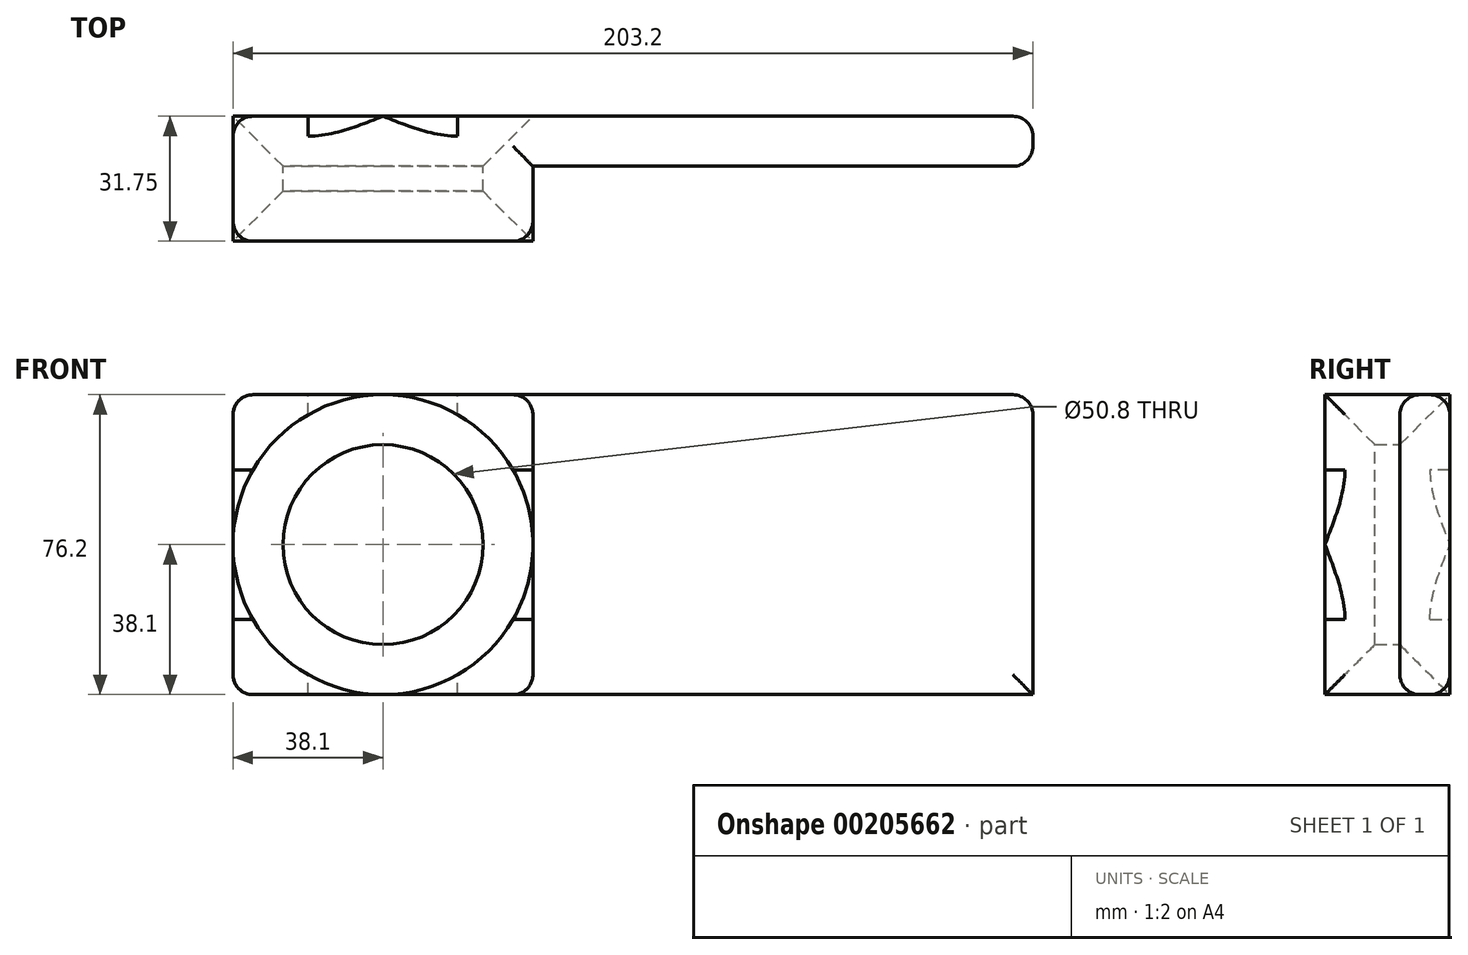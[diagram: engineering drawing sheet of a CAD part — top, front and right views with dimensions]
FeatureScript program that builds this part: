
annotation { "Feature Type Name" : "Feature", "Feature Type Description" : "" }
export const myFeature = defineFeature(function(context is Context, id is Id, definition is map)
    precondition{}
    {
        {
            var Q0;
            Q0=qCreatedBy(makeId("Front.planeOp"),FACE);
            var sketch = newSketch(context, id + "F0", { "sketchPlane" : qUnion([Q0])});
            skLineSegment(sketch, "E0.bottom", {"start": v(101.6, 38.1) * mm, "end": v(-101.6, 38.1) * mm});
            skLineSegment(sketch, "E0.top", {"start": v(101.6, -38.1) * mm, "end": v(-101.6, -38.1) * mm});
            skLineSegment(sketch, "E0.left", {"start": v(101.6, 38.1) * mm, "end": v(101.6, -38.1) * mm});
            skLineSegment(sketch, "E0.right", {"start": v(-101.6, 38.1) * mm, "end": v(-101.6, -38.1) * mm});
            skPoint(sketch, "E0.middle", {"position": v(0, 0) * mm});
            skLineSegment(sketch, "E1", {"start": v(-101.6, 0) * mm, "end": v(101.6, 0) * mm, "construction": true});
            skLineSegment(sketch, "E2", {"start": v(-63.5, 38.1) * mm, "end": v(-63.5, -38.1) * mm, "construction": true});
            skLineSegment(sketch, "E3.bottom", {"start": v(-25.4, 38.1) * mm, "end": v(-101.6, 38.1) * mm});
            skLineSegment(sketch, "E3.top", {"start": v(-25.4, -38.1) * mm, "end": v(-101.6, -38.1) * mm});
            skPoint(sketch, "E3.middle", {"position": v(-63.5, 0) * mm});
            skCircle(sketch, "E4", {"center": v(-63.5, 0) * mm, "radius": 25.4 * mm});
            skLineSegment(sketch, "E5.left", {"start": v(-25.4, 38.1) * mm, "end": v(-25.4, -38.1) * mm});
            skSolve(sketch);
        }
        {
            var Q0;
            Q0 = qSketchRegion(id + "F0", true);
            extrude(context, id + "F1", {"entities" : qUnion([Q0]), "endBound" : BoundingType.SYMMETRIC, "depth" : 12.7 * mm});
        }
        {
            var Q0;
            Q0=makeQuery(id+"F0.imprint","IMPRINT",FACE,{"disambiguationData":[TD([[makeQuery(id+"F0.imprint","IMPRINT",EDGE,{"derivedFrom":sQuery(id+"F0.wireOp",EDGE,"E4")}),-1.0]])]});
            extrude(context, id + "F2", {"entities" : qUnion([Q0]), "operationType" : NewBodyOperationType.ADD, "depth" : 25.4 * mm});
        }
        {
            var Q0;
            Q0=makeQuery(id+"F2.opExtrude","CAP_EDGE",EDGE,{"disambiguationData":[OSD([sQuery(id+"F0.wireOp",EDGE,"E4")])],"isStart":false});
            var Q1;
            Q1=makeQuery(id+"F1.opExtrude","CAP_EDGE",EDGE,{"disambiguationData":[OSD([sQuery(id+"F0.wireOp",EDGE,"E4")])],"isStart":true});
            chamfer(context, id + "F3", {"entities" : qUnion([Q0, Q1]), "width" : 12.7 * mm, "tangentPropagation" : true});
        }
        {
            var Q0;
            Q0=makeQuery(id+"F2.opExtrude","CAP_EDGE",EDGE,{"disambiguationData":[OSD([sQuery(id+"F0.wireOp",EDGE,"E0.right")])],"isStart":false});
            var Q1;
            Q1=makeQuery(id+"F2.opExtrude","CAP_EDGE",EDGE,{"disambiguationData":[OSD([sQuery(id+"F0.wireOp",EDGE,"E3.top")])],"isStart":false});
            var Q2;
            Q2=makeQuery(id+"F2.opExtrude","CAP_EDGE",EDGE,{"disambiguationData":[OSD([sQuery(id+"F0.wireOp",EDGE,"E3.bottom")])],"isStart":false});
            var Q3;
            Q3=makeQuery(id+"F2.opExtrude","CAP_EDGE",EDGE,{"disambiguationData":[OSD([sQuery(id+"F0.wireOp",EDGE,"E5.left")])],"isStart":false});
            var Q4;
            {var subQ0=sQuery(id+"F0.wireOp",EDGE,"E0.right");var subQ1=sQuery(id+"F0.wireOp",EDGE,"E3.top");Q4=makeQuery(id+"F2.boolean.opBoolean","MERGE",EDGE,{"derivedFrom":[makeQuery(id+"F1.opExtrude","SWEPT_EDGE",EDGE,{"disambiguationData":[OSD([subQ1,subQ0])]}),makeQuery(id+"F2.opExtrude","SWEPT_EDGE",EDGE,{"disambiguationData":[OSD([subQ1,subQ0])]})]});}
            var Q5;
            Q5=makeQuery(id+"F1.opExtrude","CAP_EDGE",EDGE,{"disambiguationData":[OSD([sQuery(id+"F0.wireOp",EDGE,"E0.right")])],"isStart":true});
            var Q6;
            Q6=makeQuery(id+"F1.opExtrude","CAP_EDGE",EDGE,{"disambiguationData":[OSD([sQuery(id+"F0.wireOp",EDGE,"E0.top"),sQuery(id+"F0.wireOp",EDGE,"E3.top")])],"isStart":true});
            var Q7;
            Q7=makeQuery(id+"F1.opExtrude","CAP_EDGE",EDGE,{"disambiguationData":[OSD([sQuery(id+"F0.wireOp",EDGE,"E0.bottom"),sQuery(id+"F0.wireOp",EDGE,"E3.bottom")])],"isStart":true});
            var Q8;
            Q8=makeQuery(id+"F1.opExtrude","CAP_EDGE",EDGE,{"disambiguationData":[OSD([sQuery(id+"F0.wireOp",EDGE,"E0.left")])],"isStart":true});
            var Q9;
            Q9=makeQuery(id+"F1.opExtrude","SWEPT_EDGE",EDGE,{"disambiguationData":[OSD([sQuery(id+"F0.wireOp",EDGE,"E0.bottom"),sQuery(id+"F0.wireOp",EDGE,"E0.left")])]});
            var Q10;
            Q10=makeQuery(id+"F1.opExtrude","CAP_EDGE",EDGE,{"disambiguationData":[OSD([sQuery(id+"F0.wireOp",EDGE,"E0.left")])],"isStart":false});
            var Q11;
            Q11=makeQuery(id+"F1.opExtrude","CAP_EDGE",EDGE,{"disambiguationData":[OSD([sQuery(id+"F0.wireOp",EDGE,"E0.bottom"),sQuery(id+"F0.wireOp",EDGE,"E3.bottom")])],"isStart":false});
            var Q12;
            Q12=makeQuery(id+"F1.opExtrude","CAP_EDGE",EDGE,{"disambiguationData":[OSD([sQuery(id+"F0.wireOp",EDGE,"E0.top"),sQuery(id+"F0.wireOp",EDGE,"E3.top")])],"isStart":false});
            var Q13;
            Q13=makeQuery(id+"F2.opExtrude","SWEPT_EDGE",EDGE,{"disambiguationData":[OSD([sQuery(id+"F0.wireOp",EDGE,"E0.top"),sQuery(id+"F0.wireOp",EDGE,"E3.top"),sQuery(id+"F0.wireOp",EDGE,"E5.left")])]});
            var Q14;
            Q14=makeQuery(id+"F2.opExtrude","SWEPT_EDGE",EDGE,{"disambiguationData":[OSD([sQuery(id+"F0.wireOp",EDGE,"E0.bottom"),sQuery(id+"F0.wireOp",EDGE,"E3.bottom"),sQuery(id+"F0.wireOp",EDGE,"E5.left")])]});
            var Q15;
            {var subQ0=sQuery(id+"F0.wireOp",EDGE,"E0.right");var subQ1=sQuery(id+"F0.wireOp",EDGE,"E3.bottom");Q15=makeQuery(id+"F2.boolean.opBoolean","MERGE",EDGE,{"derivedFrom":[makeQuery(id+"F1.opExtrude","SWEPT_EDGE",EDGE,{"disambiguationData":[OSD([subQ1,subQ0])]}),makeQuery(id+"F2.opExtrude","SWEPT_EDGE",EDGE,{"disambiguationData":[OSD([subQ1,subQ0])]})]});}
            fillet(context, id + "F4", {"entities" : qUnion([Q0, Q1, Q2, Q3, Q4, Q5, Q6, Q7, Q8, Q9, Q10, Q11, Q12, Q13, Q14, Q15]), "radius" : 5.08 * mm, "tangentPropagation" : true, "allowEdgeOverflow" : false});
        }
    });
